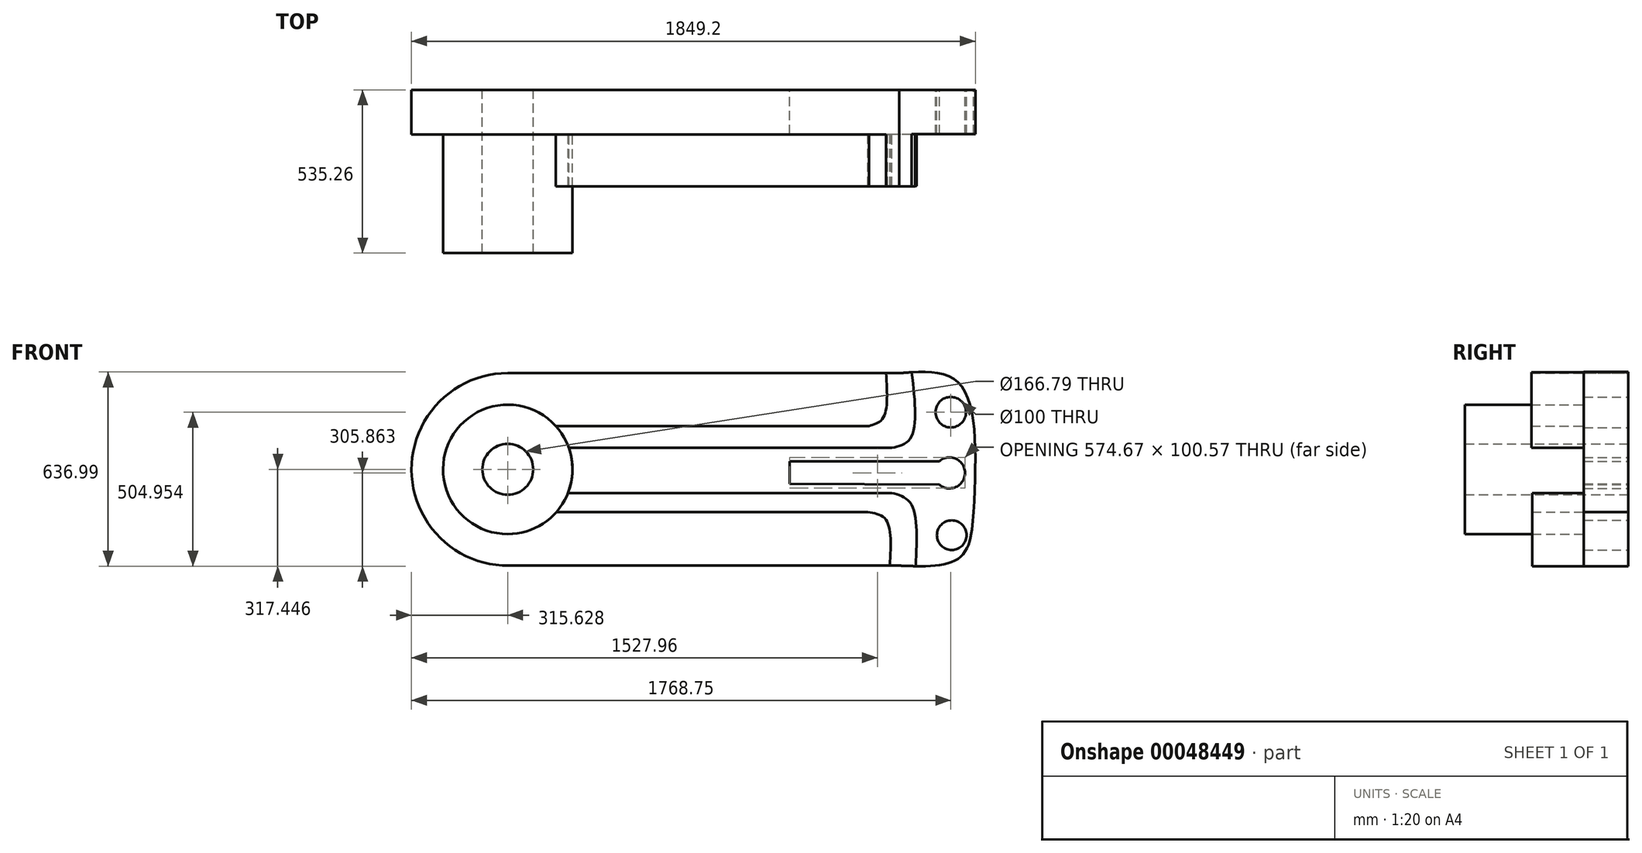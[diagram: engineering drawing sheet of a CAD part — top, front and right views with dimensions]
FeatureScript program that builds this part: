
annotation { "Feature Type Name" : "Feature", "Feature Type Description" : "" }
export const myFeature = defineFeature(function(context is Context, id is Id, definition is map)
    precondition{}
    {
        {
            var Q0;
            Q0=qCreatedBy(makeId("Front.planeOp"),FACE);
            var sketch = newSketch(context, id + "F0", { "sketchPlane" : qUnion([Q0])});
            skLineSegment(sketch, "E0", {"start": v(829.41, -175.5) * mm, "end": v(-451.84, -175.5) * mm});
            skLineSegment(sketch, "E1", {"start": v(829.41, 455.76) * mm, "end": v(-454.96, 455.76) * mm});
            skFitSpline(sketch, "E2", {"points": [v(829.41, 455.76) * mm, v(1026.29, 421.38) * mm, v(1073.16, 0) * mm], "startDerivative": vector(565.97, 43.02) * mm, "endDerivative": vector(-40.88, -896.35) * mm});
            skFitSpline(sketch, "E3", {"points": [v(829.41, -175.5) * mm, v(1029.41, -147.37) * mm, v(1073.16, 0) * mm], "startDerivative": vector(449.41, -17.73) * mm, "endDerivative": vector(28.53, 377.7) * mm});
            skArc(sketch, "E4", {"start": v(-454.96, 455.76) * mm, "mid": v(-770.6, 138.56) * mm, "end": v(-451.84, -175.5) * mm});
            skCircle(sketch, "E5", {"center": v(-454.96, 140.13) * mm, "radius": 83.4 * mm});
            skCircle(sketch, "E6", {"center": v(-454.96, 140.13) * mm, "radius": 212.23 * mm});
            skLineSegment(sketch, "E7", {"start": v(-297.48, 282.4) * mm, "end": v(729.41, 282.4) * mm});
            skFitSpline(sketch, "E8", {"points": [v(729.41, 282.4) * mm, v(776.29, 308.88) * mm, v(785.66, 455.76) * mm], "startDerivative": vector(144.98, 39.08) * mm, "endDerivative": vector(-19.02, 287.25) * mm});
            skCircle(sketch, "E9", {"center": v(998.16, 327.63) * mm, "radius": 50 * mm});
            skCircle(sketch, "E10", {"center": v(1001.29, -75.5) * mm, "radius": 48.51 * mm});
            skLineSegment(sketch, "E11", {"start": v(-295.57, 0) * mm, "end": v(726.29, 0) * mm});
            skFitSpline(sketch, "E12", {"points": [v(726.29, 0) * mm, v(785.66, -25.5) * mm, v(798.16, -175.5) * mm], "startDerivative": vector(175.59, -28) * mm, "endDerivative": vector(-18.37, -303.83) * mm});
            skLineSegment(sketch, "E13", {"start": v(-254.83, 210.77) * mm, "end": v(804.41, 210.77) * mm});
            skLineSegment(sketch, "E14", {"start": v(-257.26, 62.96) * mm, "end": v(804.41, 62.96) * mm});
            skFitSpline(sketch, "E15", {"points": [v(804.41, 210.77) * mm, v(866.91, 243.26) * mm, v(870.17, 458.58) * mm], "startDerivative": vector(202.07, 43.96) * mm, "endDerivative": vector(-47.86, 417.56) * mm});
            skFitSpline(sketch, "E16", {"points": [v(804.41, 62.96) * mm, v(866.91, 27.63) * mm, v(883.1, -177.2) * mm], "startDerivative": vector(194.72, -52.22) * mm, "endDerivative": vector(-19.02, -398.62) * mm});
            skArc(sketch, "E17", {"start": v(960.66, 90.13) * mm, "mid": v(1044.7, 128.54) * mm, "end": v(960.66, 166.95) * mm});
            skLineSegment(sketch, "E18", {"start": v(960.66, 166.95) * mm, "end": v(470.04, 166.95) * mm});
            skLineSegment(sketch, "E19", {"start": v(470.04, 166.95) * mm, "end": v(470.04, 93.26) * mm});
            skLineSegment(sketch, "E20", {"start": v(470.04, 93.26) * mm, "end": v(960.66, 90.13) * mm});
            skLineSegment(sketch, "E21", {"start": v(-629.75, 402.95) * mm, "end": v(26.47, 402.95) * mm, "construction": true});
            skLineSegment(sketch, "E22", {"start": v(26.47, 402.95) * mm, "end": v(26.47, 455.76) * mm, "construction": true});
            skLineSegment(sketch, "E23", {"start": v(-629.75, -122.7) * mm, "end": v(28.96, -122.7) * mm, "construction": true});
            skLineSegment(sketch, "E24", {"start": v(28.96, -122.7) * mm, "end": v(28.96, -175.5) * mm});
            skCircle(sketch, "E25", {"center": v(-454.96, 140.13) * mm, "radius": 120.7 * mm, "construction": true});
            skSolve(sketch);
        }
        {
            var Q0;
            {var subQ8=sQuery(id+"F0.wireOp",EDGE,"E4");Q0=makeQuery(id+"F0.imprint","IMPRINT",FACE,{"disambiguationData":[TD([[makeQuery(id+"F0.imprint","IMPRINT",EDGE,{"derivedFrom":subQ8}),1.0]])]});}
            extrude(context, id + "F1", {"entities" : qUnion([Q0]), "depth" : 146.4 * mm});
        }
        {
            var Q0;
            Q0=makeQuery(id+"F0.imprint","IMPRINT",FACE,{"disambiguationData":[TD([[makeQuery(id+"F0.imprint","IMPRINT",EDGE,{"derivedFrom":sQuery(id+"F0.wireOp",EDGE,"E5")}),-1.0]])]});
            extrude(context, id + "F2", {"entities" : qUnion([Q0]), "operationType" : NewBodyOperationType.ADD, "depth" : 535.26 * mm});
        }
        {
            var Q0;
            {var subQ6=sQuery(id+"F0.wireOp",EDGE,"E11");Q0=makeQuery(id+"F0.imprint","IMPRINT",FACE,{"disambiguationData":[TD([[makeQuery(id+"F0.imprint","IMPRINT",EDGE,{"derivedFrom":subQ6}),1.0]])]});}
            extrude(context, id + "F3", {"entities" : qUnion([Q0]), "operationType" : NewBodyOperationType.ADD, "depth" : 314.9 * mm});
        }
        {
            var Q0;
            {var subQ7=sQuery(id+"F0.wireOp",EDGE,"E7");Q0=makeQuery(id+"F0.imprint","IMPRINT",FACE,{"disambiguationData":[TD([[makeQuery(id+"F0.imprint","IMPRINT",EDGE,{"derivedFrom":subQ7}),-1.0]])]});}
            extrude(context, id + "F4", {"entities" : qUnion([Q0]), "operationType" : NewBodyOperationType.ADD, "depth" : 317.18 * mm});
        }
        {
            var Q0;
            Q0=makeQuery(id+"F0.imprint","IMPRINT",FACE,{"disambiguationData":[TD([[makeQuery(id+"F0.imprint","IMPRINT",EDGE,{"derivedFrom":sQuery(id+"F0.wireOp",EDGE,"E9")}),-1.0]])]});
            extrude(context, id + "F5", {"entities" : qUnion([Q0]), "operationType" : NewBodyOperationType.ADD, "depth" : 145.32 * mm});
        }
    });
